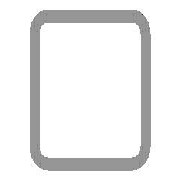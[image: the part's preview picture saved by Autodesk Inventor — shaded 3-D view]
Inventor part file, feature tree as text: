
AUTODESK INVENTOR PART (.ipt)
format: ipt  version: 2025.1 (Build 291241020, 241B)  size: 134,144 bytes
history: native  units: mm (DEFAULTED — no unit token found)
features: other x4, sketch x1, plane x1
ambient origin geometry x8: Origin, YZ Plane, XZ Plane, XY Plane, X Axis, Y Axis, Z Axis, Center Point
bodies: Solid1 (feature_tree), Body (feature_tree)
feature tree (6):
  parser-record x1  (decoder bookkeeping rows leaked as tree rows — omitted from the tree; the rows remain in map.json)
  other  "Driven Length"
  other  "Start Plane"
  other  "End Plane"
  sketch  "Sketch3"  dims[d3=6500.0mm d4=0.0mm d7=6.0mm d9=100.0mm d11=100.0mm d12=3.0mm d13=-0.0mm d14=6500.0mm d15=50.0mm d16=50.0mm d17=90.0deg d18=6500.0mm]
  plane  "Work Plane3"
